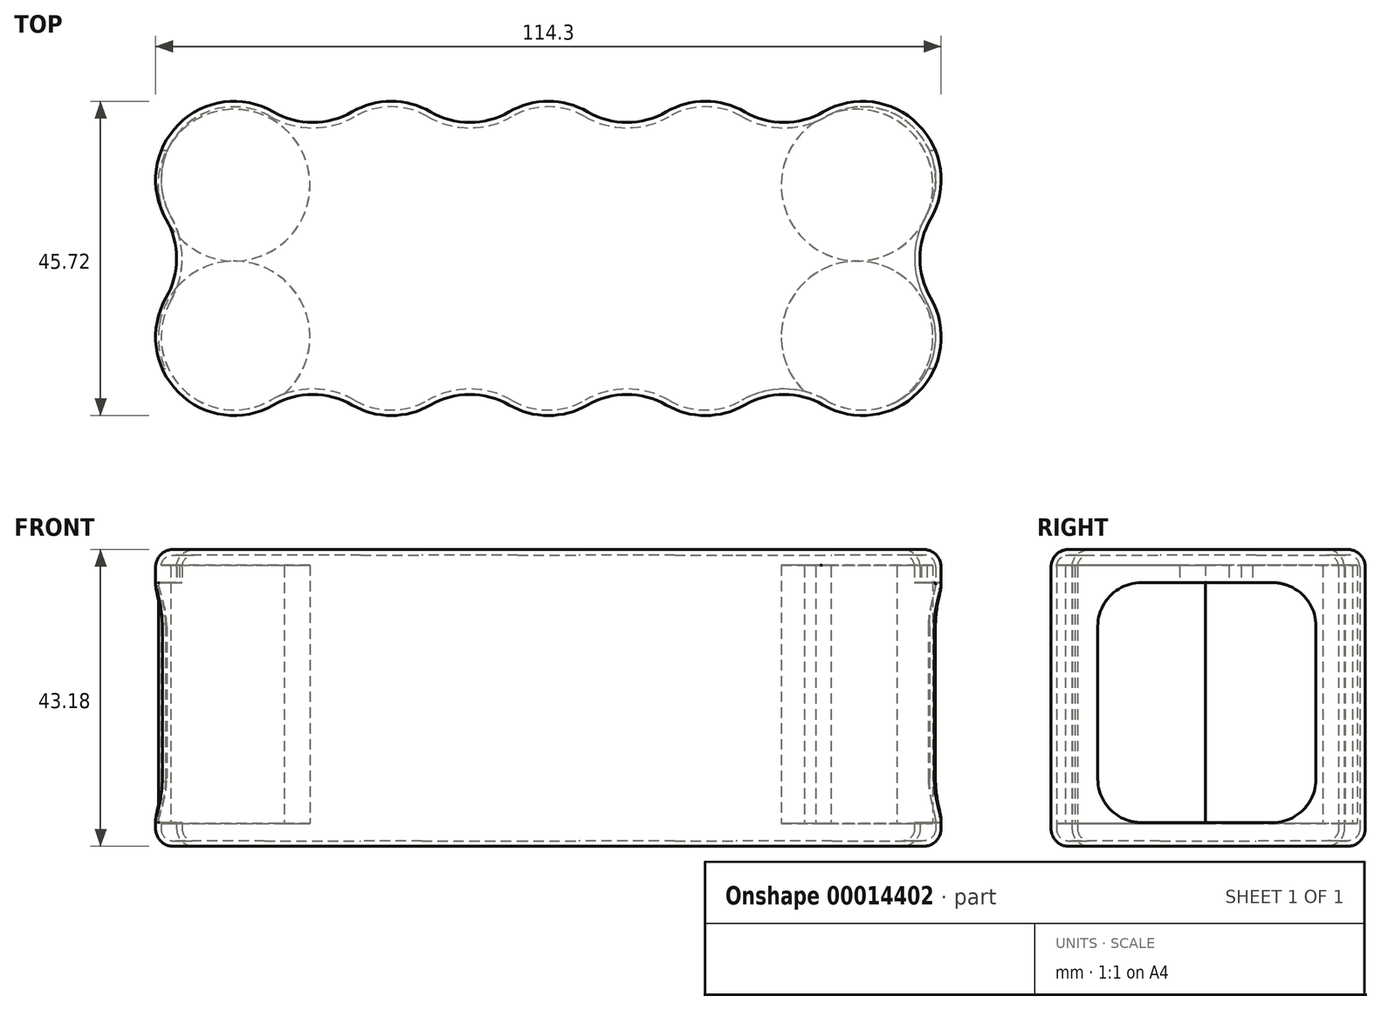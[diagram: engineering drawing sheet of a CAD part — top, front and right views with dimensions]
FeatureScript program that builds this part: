
annotation { "Feature Type Name" : "Feature", "Feature Type Description" : "" }
export const myFeature = defineFeature(function(context is Context, id is Id, definition is map)
    precondition{}
    {
        {
            var Q0;
            Q0=qCreatedBy(makeId("Top.planeOp"),FACE);
            var sketch = newSketch(context, id + "F0", { "sketchPlane" : qUnion([Q0])});
            skArc(sketch, "E0", {"start": v(-9.9, 5.71) * mm, "mid": v(-8.08, -8.08) * mm, "end": v(5.71, -9.9) * mm});
            skArc(sketch, "E1.1.0.0", {"start": v(17.14, -9.9) * mm, "mid": v(22.86, -11.43) * mm, "end": v(28.57, -9.9) * mm});
            skArc(sketch, "E1.2.0.0", {"start": v(40, -9.9) * mm, "mid": v(45.72, -11.43) * mm, "end": v(51.43, -9.9) * mm});
            skArc(sketch, "E1.3.0.0", {"start": v(62.86, -9.9) * mm, "mid": v(68.58, -11.43) * mm, "end": v(74.3, -9.9) * mm});
            skArc(sketch, "E1.4.0.0", {"start": v(85.72, -9.9) * mm, "mid": v(99.52, -8.08) * mm, "end": v(101.34, 5.71) * mm});
            skLineSegment(sketch, "E1.direction1", {"start": v(0, 0) * mm, "end": v(22.86, 0) * mm, "construction": true});
            skArc(sketch, "E2", {"start": v(17.14, -9.9) * mm, "mid": v(11.43, -8.37) * mm, "end": v(5.71, -9.9) * mm});
            skPoint(sketch, "E3.orphan", {"position": v(11.43, 0) * mm});
            skArc(sketch, "E4.1.0.0", {"start": v(40, -9.9) * mm, "mid": v(34.29, -8.37) * mm, "end": v(28.57, -9.9) * mm});
            skArc(sketch, "E4.2.0.0", {"start": v(62.86, -9.9) * mm, "mid": v(57.15, -8.37) * mm, "end": v(51.43, -9.9) * mm});
            skArc(sketch, "E4.3.0.0", {"start": v(85.72, -9.9) * mm, "mid": v(80, -8.37) * mm, "end": v(74.3, -9.9) * mm});
            skLineSegment(sketch, "E5", {"start": v(0, 11.43) * mm, "end": v(91.44, 11.43) * mm, "construction": true});
            skArc(sketch, "E6.0.MirrorCS", {"start": v(17.14, 32.76) * mm, "mid": v(22.86, 34.3) * mm, "end": v(28.57, 32.76) * mm});
            skArc(sketch, "E6.1.MirrorCS", {"start": v(85.72, 32.76) * mm, "mid": v(99.52, 30.94) * mm, "end": v(101.34, 17.15) * mm});
            skPoint(sketch, "E6.2.MirrorP", {"position": v(11.43, 22.86) * mm});
            skArc(sketch, "E6.3.MirrorCS", {"start": v(17.14, 32.76) * mm, "mid": v(11.43, 31.23) * mm, "end": v(5.72, 32.76) * mm});
            skArc(sketch, "E6.4.MirrorCS", {"start": v(62.86, 32.76) * mm, "mid": v(57.15, 31.23) * mm, "end": v(51.43, 32.76) * mm});
            skArc(sketch, "E6.5.MirrorCS", {"start": v(40, 32.76) * mm, "mid": v(45.72, 34.3) * mm, "end": v(51.43, 32.76) * mm});
            skArc(sketch, "E6.6.MirrorCS", {"start": v(62.86, 32.76) * mm, "mid": v(68.58, 34.3) * mm, "end": v(74.3, 32.76) * mm});
            skArc(sketch, "E6.7.MirrorCS", {"start": v(85.72, 32.76) * mm, "mid": v(80, 31.23) * mm, "end": v(74.3, 32.76) * mm});
            skArc(sketch, "E6.8.MirrorCS", {"start": v(40, 32.76) * mm, "mid": v(34.29, 31.23) * mm, "end": v(28.57, 32.76) * mm});
            skArc(sketch, "E6.9.MirrorCS", {"start": v(-9.9, 17.14) * mm, "mid": v(-8.08, 30.94) * mm, "end": v(5.71, 32.76) * mm});
            skArc(sketch, "E7", {"start": v(-9.9, 5.71) * mm, "mid": v(-8.37, 11.43) * mm, "end": v(-9.9, 17.14) * mm});
            skLineSegment(sketch, "E8", {"start": v(45.72, 22.86) * mm, "end": v(45.72, 0) * mm, "construction": true});
            skArc(sketch, "E9.0.MirrorCS", {"start": v(101.34, 5.71) * mm, "mid": v(99.8, 11.43) * mm, "end": v(101.34, 17.15) * mm});
            skSolve(sketch);
        }
        {
            var Q0;
            Q0=qSketchRegion(id+"F0",true);
            extrude(context, id + "F1", {"entities" : qUnion([Q0]), "depth" : 43.18 * mm});
        }
        {
            var Q0;
            Q0=makeQuery(id+"F1.opExtrude","CAP_EDGE",EDGE,{"disambiguationData":[OSD([sQuery(id+"F0.wireOp",EDGE,"E6.6.MirrorCS")])],"isStart":false});
            var Q1;
            Q1=makeQuery(id+"F1.opExtrude","SWEPT_EDGE",EDGE,{"disambiguationData":[OSD([sQuery(id+"F0.wireOp",EDGE,"E6.4.MirrorCS"),sQuery(id+"F0.wireOp",EDGE,"E6.6.MirrorCS")])]});
            var Q2;
            Q2=makeQuery(id+"F1.opExtrude","SWEPT_FACE",FACE,{"disambiguationData":[OSD([sQuery(id+"F0.wireOp",EDGE,"E6.4.MirrorCS")])]});
            var Q3;
            Q3=makeQuery(id+"F1.opExtrude","SWEPT_EDGE",EDGE,{"disambiguationData":[OSD([sQuery(id+"F0.wireOp",EDGE,"E6.5.MirrorCS"),sQuery(id+"F0.wireOp",EDGE,"E6.8.MirrorCS")])]});
            var Q4;
            Q4=makeQuery(id+"F1.opExtrude","SWEPT_FACE",FACE,{"disambiguationData":[OSD([sQuery(id+"F0.wireOp",EDGE,"E9.0.MirrorCS")])]});
            var Q5;
            Q5=makeQuery(id+"F1.opExtrude","CAP_EDGE",EDGE,{"disambiguationData":[OSD([sQuery(id+"F0.wireOp",EDGE,"E6.1.MirrorCS")])],"isStart":true});
            var Q6;
            Q6=makeQuery(id+"F1.opExtrude","CAP_EDGE",EDGE,{"disambiguationData":[OSD([sQuery(id+"F0.wireOp",EDGE,"E1.2.0.0")])],"isStart":true});
            var Q7;
            Q7=makeQuery(id+"F1.opExtrude","SWEPT_FACE",FACE,{"disambiguationData":[OSD([sQuery(id+"F0.wireOp",EDGE,"E0")])]});
            var Q8;
            Q8=makeQuery(id+"F1.opExtrude","SWEPT_FACE",FACE,{"disambiguationData":[OSD([sQuery(id+"F0.wireOp",EDGE,"E6.3.MirrorCS")])]});
            var Q9;
            Q9=makeQuery(id+"F1.opExtrude","SWEPT_EDGE",EDGE,{"disambiguationData":[OSD([sQuery(id+"F0.wireOp",EDGE,"E6.3.MirrorCS"),sQuery(id+"F0.wireOp",EDGE,"E6.9.MirrorCS")])]});
            var Q10;
            Q10=makeQuery(id+"F1.opExtrude","SWEPT_FACE",FACE,{"disambiguationData":[OSD([sQuery(id+"F0.wireOp",EDGE,"E6.5.MirrorCS")])]});
            var Q11;
            Q11=makeQuery(id+"F1.opExtrude","CAP_EDGE",EDGE,{"disambiguationData":[OSD([sQuery(id+"F0.wireOp",EDGE,"E6.7.MirrorCS")])],"isStart":false});
            var Q12;
            Q12=makeQuery(id+"F1.opExtrude","SWEPT_FACE",FACE,{"disambiguationData":[OSD([sQuery(id+"F0.wireOp",EDGE,"E6.7.MirrorCS")])]});
            var Q13;
            Q13=makeQuery(id+"F1.opExtrude","CAP_EDGE",EDGE,{"disambiguationData":[OSD([sQuery(id+"F0.wireOp",EDGE,"E6.3.MirrorCS")])],"isStart":false});
            var Q14;
            Q14=makeQuery(id+"F1.opExtrude","CAP_EDGE",EDGE,{"disambiguationData":[OSD([sQuery(id+"F0.wireOp",EDGE,"E6.5.MirrorCS")])],"isStart":true});
            var Q15;
            Q15=makeQuery(id+"F1.opExtrude","SWEPT_FACE",FACE,{"disambiguationData":[OSD([sQuery(id+"F0.wireOp",EDGE,"E6.9.MirrorCS")])]});
            var Q16;
            Q16=makeQuery(id+"F1.opExtrude","CAP_EDGE",EDGE,{"disambiguationData":[OSD([sQuery(id+"F0.wireOp",EDGE,"E0")])],"isStart":true});
            var Q17;
            Q17=makeQuery(id+"F1.opExtrude","CAP_EDGE",EDGE,{"disambiguationData":[OSD([sQuery(id+"F0.wireOp",EDGE,"E6.8.MirrorCS")])],"isStart":true});
            var Q18;
            Q18=makeQuery(id+"F1.opExtrude","SWEPT_FACE",FACE,{"disambiguationData":[OSD([sQuery(id+"F0.wireOp",EDGE,"E6.1.MirrorCS")])]});
            var Q19;
            Q19=makeQuery(id+"F1.opExtrude","SWEPT_FACE",FACE,{"disambiguationData":[OSD([sQuery(id+"F0.wireOp",EDGE,"E6.0.MirrorCS")])]});
            var Q20;
            Q20=makeQuery(id+"F1.opExtrude","CAP_EDGE",EDGE,{"disambiguationData":[OSD([sQuery(id+"F0.wireOp",EDGE,"E6.1.MirrorCS")])],"isStart":false});
            var Q21;
            Q21=makeQuery(id+"F1.opExtrude","SWEPT_FACE",FACE,{"disambiguationData":[OSD([sQuery(id+"F0.wireOp",EDGE,"E4.3.0.0")])]});
            var Q22;
            Q22=makeQuery(id+"F1.opExtrude","SWEPT_EDGE",EDGE,{"disambiguationData":[OSD([sQuery(id+"F0.wireOp",EDGE,"E6.0.MirrorCS"),sQuery(id+"F0.wireOp",EDGE,"E6.3.MirrorCS")])]});
            var Q23;
            Q23=makeQuery(id+"F1.opExtrude","SWEPT_FACE",FACE,{"disambiguationData":[OSD([sQuery(id+"F0.wireOp",EDGE,"E4.2.0.0")])]});
            var Q24;
            Q24=makeQuery(id+"F1.opExtrude","CAP_EDGE",EDGE,{"disambiguationData":[OSD([sQuery(id+"F0.wireOp",EDGE,"E6.9.MirrorCS")])],"isStart":false});
            var Q25;
            Q25=makeQuery(id+"F1.opExtrude","SWEPT_FACE",FACE,{"disambiguationData":[OSD([sQuery(id+"F0.wireOp",EDGE,"E4.1.0.0")])]});
            var Q26;
            Q26=makeQuery(id+"F1.opExtrude","CAP_EDGE",EDGE,{"disambiguationData":[OSD([sQuery(id+"F0.wireOp",EDGE,"E6.9.MirrorCS")])],"isStart":true});
            var Q27;
            Q27=makeQuery(id+"F1.opExtrude","CAP_EDGE",EDGE,{"disambiguationData":[OSD([sQuery(id+"F0.wireOp",EDGE,"E6.0.MirrorCS")])],"isStart":true});
            var Q28;
            Q28=makeQuery(id+"F1.opExtrude","SWEPT_FACE",FACE,{"disambiguationData":[OSD([sQuery(id+"F0.wireOp",EDGE,"E2")])]});
            var Q29;
            Q29=makeQuery(id+"F1.opExtrude","SWEPT_FACE",FACE,{"disambiguationData":[OSD([sQuery(id+"F0.wireOp",EDGE,"E1.4.0.0")])]});
            var Q30;
            Q30=makeQuery(id+"F1.opExtrude","SWEPT_FACE",FACE,{"disambiguationData":[OSD([sQuery(id+"F0.wireOp",EDGE,"E7")])]});
            var Q31;
            Q31=makeQuery(id+"F1.opExtrude","CAP_FACE",FACE,{"disambiguationData":[OSD([sQuery(id+"F0.wireOp",EDGE,"E0"),sQuery(id+"F0.wireOp",EDGE,"E1.1.0.0"),sQuery(id+"F0.wireOp",EDGE,"E1.2.0.0"),sQuery(id+"F0.wireOp",EDGE,"E1.3.0.0"),sQuery(id+"F0.wireOp",EDGE,"E1.4.0.0"),sQuery(id+"F0.wireOp",EDGE,"E2"),sQuery(id+"F0.wireOp",EDGE,"E4.1.0.0"),sQuery(id+"F0.wireOp",EDGE,"E4.2.0.0"),sQuery(id+"F0.wireOp",EDGE,"E4.3.0.0"),sQuery(id+"F0.wireOp",EDGE,"E6.0.MirrorCS"),sQuery(id+"F0.wireOp",EDGE,"E6.1.MirrorCS"),sQuery(id+"F0.wireOp",EDGE,"E6.3.MirrorCS"),sQuery(id+"F0.wireOp",EDGE,"E6.4.MirrorCS"),sQuery(id+"F0.wireOp",EDGE,"E6.5.MirrorCS"),sQuery(id+"F0.wireOp",EDGE,"E6.6.MirrorCS"),sQuery(id+"F0.wireOp",EDGE,"E6.7.MirrorCS"),sQuery(id+"F0.wireOp",EDGE,"E6.8.MirrorCS"),sQuery(id+"F0.wireOp",EDGE,"E6.9.MirrorCS"),sQuery(id+"F0.wireOp",EDGE,"E7"),sQuery(id+"F0.wireOp",EDGE,"E9.0.MirrorCS")])],"isStart":false});
            var Q32;
            Q32=makeQuery(id+"F1.opExtrude","CAP_FACE",FACE,{"disambiguationData":[OSD([sQuery(id+"F0.wireOp",EDGE,"E0"),sQuery(id+"F0.wireOp",EDGE,"E1.1.0.0"),sQuery(id+"F0.wireOp",EDGE,"E1.2.0.0"),sQuery(id+"F0.wireOp",EDGE,"E1.3.0.0"),sQuery(id+"F0.wireOp",EDGE,"E1.4.0.0"),sQuery(id+"F0.wireOp",EDGE,"E2"),sQuery(id+"F0.wireOp",EDGE,"E4.1.0.0"),sQuery(id+"F0.wireOp",EDGE,"E4.2.0.0"),sQuery(id+"F0.wireOp",EDGE,"E4.3.0.0"),sQuery(id+"F0.wireOp",EDGE,"E6.0.MirrorCS"),sQuery(id+"F0.wireOp",EDGE,"E6.1.MirrorCS"),sQuery(id+"F0.wireOp",EDGE,"E6.3.MirrorCS"),sQuery(id+"F0.wireOp",EDGE,"E6.4.MirrorCS"),sQuery(id+"F0.wireOp",EDGE,"E6.5.MirrorCS"),sQuery(id+"F0.wireOp",EDGE,"E6.6.MirrorCS"),sQuery(id+"F0.wireOp",EDGE,"E6.7.MirrorCS"),sQuery(id+"F0.wireOp",EDGE,"E6.8.MirrorCS"),sQuery(id+"F0.wireOp",EDGE,"E6.9.MirrorCS"),sQuery(id+"F0.wireOp",EDGE,"E7"),sQuery(id+"F0.wireOp",EDGE,"E9.0.MirrorCS")])],"isStart":true});
            var Q33;
            Q33=makeQuery(id+"F1.opExtrude","CAP_EDGE",EDGE,{"disambiguationData":[OSD([sQuery(id+"F0.wireOp",EDGE,"E6.8.MirrorCS")])],"isStart":false});
            var Q34;
            Q34=makeQuery(id+"F1.opExtrude","CAP_EDGE",EDGE,{"disambiguationData":[OSD([sQuery(id+"F0.wireOp",EDGE,"E6.3.MirrorCS")])],"isStart":true});
            var Q35;
            Q35=makeQuery(id+"F1.opExtrude","CAP_EDGE",EDGE,{"disambiguationData":[OSD([sQuery(id+"F0.wireOp",EDGE,"E6.4.MirrorCS")])],"isStart":false});
            var Q36;
            Q36=makeQuery(id+"F1.opExtrude","SWEPT_FACE",FACE,{"disambiguationData":[OSD([sQuery(id+"F0.wireOp",EDGE,"E6.8.MirrorCS")])]});
            var Q37;
            Q37=makeQuery(id+"F1.opExtrude","SWEPT_FACE",FACE,{"disambiguationData":[OSD([sQuery(id+"F0.wireOp",EDGE,"E6.6.MirrorCS")])]});
            var Q38;
            Q38=makeQuery(id+"F1.opExtrude","CAP_EDGE",EDGE,{"disambiguationData":[OSD([sQuery(id+"F0.wireOp",EDGE,"E1.4.0.0")])],"isStart":true});
            var Q39;
            Q39=makeQuery(id+"F1.opExtrude","CAP_EDGE",EDGE,{"disambiguationData":[OSD([sQuery(id+"F0.wireOp",EDGE,"E6.4.MirrorCS")])],"isStart":true});
            var Q40;
            Q40=makeQuery(id+"F1.opExtrude","CAP_EDGE",EDGE,{"disambiguationData":[OSD([sQuery(id+"F0.wireOp",EDGE,"E6.5.MirrorCS")])],"isStart":false});
            var Q41;
            Q41=makeQuery(id+"F1.opExtrude","SWEPT_EDGE",EDGE,{"disambiguationData":[OSD([sQuery(id+"F0.wireOp",EDGE,"E6.6.MirrorCS"),sQuery(id+"F0.wireOp",EDGE,"E6.7.MirrorCS")])]});
            var Q42;
            Q42=makeQuery(id+"F1.opExtrude","CAP_EDGE",EDGE,{"disambiguationData":[OSD([sQuery(id+"F0.wireOp",EDGE,"E6.7.MirrorCS")])],"isStart":true});
            var Q43;
            Q43=makeQuery(id+"F1.opExtrude","CAP_EDGE",EDGE,{"disambiguationData":[OSD([sQuery(id+"F0.wireOp",EDGE,"E6.6.MirrorCS")])],"isStart":true});
            var Q44;
            Q44=makeQuery(id+"F1.opExtrude","SWEPT_EDGE",EDGE,{"disambiguationData":[OSD([sQuery(id+"F0.wireOp",EDGE,"E6.1.MirrorCS"),sQuery(id+"F0.wireOp",EDGE,"E9.0.MirrorCS")])]});
            var Q45;
            Q45=makeQuery(id+"F1.opExtrude","CAP_EDGE",EDGE,{"disambiguationData":[OSD([sQuery(id+"F0.wireOp",EDGE,"E4.1.0.0")])],"isStart":false});
            var Q46;
            Q46=makeQuery(id+"F1.opExtrude","CAP_EDGE",EDGE,{"disambiguationData":[OSD([sQuery(id+"F0.wireOp",EDGE,"E1.3.0.0")])],"isStart":true});
            var Q47;
            Q47=makeQuery(id+"F1.opExtrude","CAP_EDGE",EDGE,{"disambiguationData":[OSD([sQuery(id+"F0.wireOp",EDGE,"E7")])],"isStart":true});
            var Q48;
            Q48=makeQuery(id+"F1.opExtrude","SWEPT_EDGE",EDGE,{"disambiguationData":[OSD([sQuery(id+"F0.wireOp",EDGE,"E0"),sQuery(id+"F0.wireOp",EDGE,"E7")])]});
            var Q49;
            Q49=makeQuery(id+"F1.opExtrude","CAP_EDGE",EDGE,{"disambiguationData":[OSD([sQuery(id+"F0.wireOp",EDGE,"E4.2.0.0")])],"isStart":false});
            var Q50;
            Q50=makeQuery(id+"F1.opExtrude","SWEPT_EDGE",EDGE,{"disambiguationData":[OSD([sQuery(id+"F0.wireOp",EDGE,"E6.9.MirrorCS"),sQuery(id+"F0.wireOp",EDGE,"E7")])]});
            var Q51;
            Q51=makeQuery(id+"F1.opExtrude","CAP_EDGE",EDGE,{"disambiguationData":[OSD([sQuery(id+"F0.wireOp",EDGE,"E9.0.MirrorCS")])],"isStart":false});
            var Q52;
            Q52=makeQuery(id+"F1.opExtrude","CAP_EDGE",EDGE,{"disambiguationData":[OSD([sQuery(id+"F0.wireOp",EDGE,"E1.3.0.0")])],"isStart":false});
            var Q53;
            Q53=makeQuery(id+"F1.opExtrude","CAP_EDGE",EDGE,{"disambiguationData":[OSD([sQuery(id+"F0.wireOp",EDGE,"E2")])],"isStart":true});
            var Q54;
            Q54=makeQuery(id+"F1.opExtrude","CAP_EDGE",EDGE,{"disambiguationData":[OSD([sQuery(id+"F0.wireOp",EDGE,"E4.3.0.0")])],"isStart":true});
            var Q55;
            Q55=makeQuery(id+"F1.opExtrude","SWEPT_EDGE",EDGE,{"disambiguationData":[OSD([sQuery(id+"F0.wireOp",EDGE,"E6.1.MirrorCS"),sQuery(id+"F0.wireOp",EDGE,"E6.7.MirrorCS")])]});
            var Q56;
            Q56=makeQuery(id+"F1.opExtrude","SWEPT_EDGE",EDGE,{"disambiguationData":[OSD([sQuery(id+"F0.wireOp",EDGE,"E6.0.MirrorCS"),sQuery(id+"F0.wireOp",EDGE,"E6.8.MirrorCS")])]});
            var Q57;
            Q57=makeQuery(id+"F1.opExtrude","CAP_EDGE",EDGE,{"disambiguationData":[OSD([sQuery(id+"F0.wireOp",EDGE,"E1.2.0.0")])],"isStart":false});
            var Q58;
            Q58=makeQuery(id+"F1.opExtrude","CAP_EDGE",EDGE,{"disambiguationData":[OSD([sQuery(id+"F0.wireOp",EDGE,"E7")])],"isStart":false});
            var Q59;
            Q59=makeQuery(id+"F1.opExtrude","CAP_EDGE",EDGE,{"disambiguationData":[OSD([sQuery(id+"F0.wireOp",EDGE,"E1.1.0.0")])],"isStart":false});
            var Q60;
            Q60=makeQuery(id+"F1.opExtrude","SWEPT_EDGE",EDGE,{"disambiguationData":[OSD([sQuery(id+"F0.wireOp",EDGE,"E1.4.0.0"),sQuery(id+"F0.wireOp",EDGE,"E9.0.MirrorCS")])]});
            var Q61;
            Q61=makeQuery(id+"F1.opExtrude","SWEPT_EDGE",EDGE,{"disambiguationData":[OSD([sQuery(id+"F0.wireOp",EDGE,"E1.4.0.0"),sQuery(id+"F0.wireOp",EDGE,"E4.3.0.0")])]});
            var Q62;
            Q62=makeQuery(id+"F1.opExtrude","CAP_EDGE",EDGE,{"disambiguationData":[OSD([sQuery(id+"F0.wireOp",EDGE,"E6.0.MirrorCS")])],"isStart":false});
            var Q63;
            Q63=makeQuery(id+"F1.opExtrude","SWEPT_EDGE",EDGE,{"disambiguationData":[OSD([sQuery(id+"F0.wireOp",EDGE,"E1.3.0.0"),sQuery(id+"F0.wireOp",EDGE,"E4.3.0.0")])]});
            var Q64;
            Q64=makeQuery(id+"F1.opExtrude","CAP_EDGE",EDGE,{"disambiguationData":[OSD([sQuery(id+"F0.wireOp",EDGE,"E1.1.0.0")])],"isStart":true});
            var Q65;
            Q65=makeQuery(id+"F1.opExtrude","SWEPT_EDGE",EDGE,{"disambiguationData":[OSD([sQuery(id+"F0.wireOp",EDGE,"E1.3.0.0"),sQuery(id+"F0.wireOp",EDGE,"E4.2.0.0")])]});
            var Q66;
            Q66=makeQuery(id+"F1.opExtrude","SWEPT_FACE",FACE,{"disambiguationData":[OSD([sQuery(id+"F0.wireOp",EDGE,"E1.3.0.0")])]});
            var Q67;
            Q67=makeQuery(id+"F1.opExtrude","SWEPT_FACE",FACE,{"disambiguationData":[OSD([sQuery(id+"F0.wireOp",EDGE,"E1.2.0.0")])]});
            var Q68;
            Q68=makeQuery(id+"F1.opExtrude","SWEPT_EDGE",EDGE,{"disambiguationData":[OSD([sQuery(id+"F0.wireOp",EDGE,"E1.2.0.0"),sQuery(id+"F0.wireOp",EDGE,"E4.1.0.0")])]});
            var Q69;
            Q69=makeQuery(id+"F1.opExtrude","SWEPT_FACE",FACE,{"disambiguationData":[OSD([sQuery(id+"F0.wireOp",EDGE,"E1.1.0.0")])]});
            var Q70;
            Q70=makeQuery(id+"F1.opExtrude","SWEPT_EDGE",EDGE,{"disambiguationData":[OSD([sQuery(id+"F0.wireOp",EDGE,"E1.1.0.0"),sQuery(id+"F0.wireOp",EDGE,"E4.1.0.0")])]});
            var Q71;
            Q71=makeQuery(id+"F1.opExtrude","SWEPT_EDGE",EDGE,{"disambiguationData":[OSD([sQuery(id+"F0.wireOp",EDGE,"E1.1.0.0"),sQuery(id+"F0.wireOp",EDGE,"E2")])]});
            var Q72;
            Q72=makeQuery(id+"F1.opExtrude","SWEPT_EDGE",EDGE,{"disambiguationData":[OSD([sQuery(id+"F0.wireOp",EDGE,"E0"),sQuery(id+"F0.wireOp",EDGE,"E2")])]});
            var Q73;
            Q73=makeQuery(id+"F1.opExtrude","CAP_EDGE",EDGE,{"disambiguationData":[OSD([sQuery(id+"F0.wireOp",EDGE,"E4.3.0.0")])],"isStart":false});
            var Q74;
            Q74=makeQuery(id+"F1.opExtrude","CAP_EDGE",EDGE,{"disambiguationData":[OSD([sQuery(id+"F0.wireOp",EDGE,"E0")])],"isStart":false});
            var Q75;
            Q75=makeQuery(id+"F1.opExtrude","CAP_EDGE",EDGE,{"disambiguationData":[OSD([sQuery(id+"F0.wireOp",EDGE,"E9.0.MirrorCS")])],"isStart":true});
            var Q76;
            Q76=makeQuery(id+"F1.opExtrude","CAP_EDGE",EDGE,{"disambiguationData":[OSD([sQuery(id+"F0.wireOp",EDGE,"E1.4.0.0")])],"isStart":false});
            var Q77;
            Q77=makeQuery(id+"F1.opExtrude","CAP_EDGE",EDGE,{"disambiguationData":[OSD([sQuery(id+"F0.wireOp",EDGE,"E2")])],"isStart":false});
            var Q78;
            Q78=makeQuery(id+"F1.opExtrude","CAP_EDGE",EDGE,{"disambiguationData":[OSD([sQuery(id+"F0.wireOp",EDGE,"E4.2.0.0")])],"isStart":true});
            var Q79;
            Q79=makeQuery(id+"F1.opExtrude","CAP_EDGE",EDGE,{"disambiguationData":[OSD([sQuery(id+"F0.wireOp",EDGE,"E4.1.0.0")])],"isStart":true});
            var Q80;
            Q80=makeQuery(id+"F1.opExtrude","SWEPT_EDGE",EDGE,{"disambiguationData":[OSD([sQuery(id+"F0.wireOp",EDGE,"E6.4.MirrorCS"),sQuery(id+"F0.wireOp",EDGE,"E6.5.MirrorCS")])]});
            var Q81;
            Q81=makeQuery(id+"F1.opExtrude","SWEPT_EDGE",EDGE,{"disambiguationData":[OSD([sQuery(id+"F0.wireOp",EDGE,"E1.2.0.0"),sQuery(id+"F0.wireOp",EDGE,"E4.2.0.0")])]});
            fillet(context, id + "F2", {"entities" : qUnion([Q0, Q1, Q2, Q3, Q4, Q5, Q6, Q7, Q8, Q9, Q10, Q11, Q12, Q13, Q14, Q15, Q16, Q17, Q18, Q19, Q20, Q21, Q22, Q23, Q24, Q25, Q26, Q27, Q28, Q29, Q30, Q31, Q32, Q33, Q34, Q35, Q36, Q37, Q38, Q39, Q40, Q41, Q42, Q43, Q44, Q45, Q46, Q47, Q48, Q49, Q50, Q51, Q52, Q53, Q54, Q55, Q56, Q57, Q58, Q59, Q60, Q61, Q62, Q63, Q64, Q65, Q66, Q67, Q68, Q69, Q70, Q71, Q72, Q73, Q74, Q75, Q76, Q77, Q78, Q79, Q80, Q81]), "radius" : 2.54 * mm, "tangentPropagation" : true, "allowEdgeOverflow" : false});
        }
        {
            var Q0;
            Q0=qCreatedBy(makeId("Right.planeOp"),FACE);
            var sketch = newSketch(context, id + "F3", { "sketchPlane" : qUnion([Q0])});
            skLineSegment(sketch, "E10.bottom", {"start": v(1.73, 3.44) * mm, "end": v(20.78, 3.44) * mm});
            skLineSegment(sketch, "E10.top", {"start": v(1.73, 38.37) * mm, "end": v(20.78, 38.37) * mm});
            skLineSegment(sketch, "E10.left", {"start": v(-4.62, 9.8) * mm, "end": v(-4.62, 32.02) * mm});
            skLineSegment(sketch, "E10.right", {"start": v(27.13, 9.8) * mm, "end": v(27.13, 32.02) * mm});
            skPoint(sketch, "E11.visualSharp", {"position": v(-4.62, 3.44) * mm});
            skArc(sketch, "E11.filletArc", {"start": v(-4.62, 9.8) * mm, "mid": v(-2.76, 5.3) * mm, "end": v(1.73, 3.44) * mm});
            skPoint(sketch, "E12.visualSharp", {"position": v(27.13, 3.44) * mm});
            skArc(sketch, "E12.filletArc", {"start": v(20.78, 3.44) * mm, "mid": v(25.27, 5.3) * mm, "end": v(27.13, 9.8) * mm});
            skPoint(sketch, "E13.visualSharp", {"position": v(27.13, 38.37) * mm});
            skArc(sketch, "E13.filletArc", {"start": v(27.13, 32.02) * mm, "mid": v(25.27, 36.5) * mm, "end": v(20.78, 38.37) * mm});
            skPoint(sketch, "E14.visualSharp", {"position": v(-4.62, 38.37) * mm});
            skArc(sketch, "E14.filletArc", {"start": v(1.73, 38.37) * mm, "mid": v(-2.76, 36.5) * mm, "end": v(-4.62, 32.02) * mm});
            skSolve(sketch);
        }
        {
            var Q0;
            {var subQ0=sQuery(id+"F0.wireOp",EDGE,"E7");Q0=makeQuery(id+"F2.opFillet","BLEND_FACE",FACE,{"disambiguationData":[OSD([subQ0]),TDD([makeQuery(id+"F1.opExtrude","CAP_EDGE",EDGE,{"disambiguationData":[OSD([subQ0])],"isStart":true})])]});}
            var Q1;
            {var subQ0=sQuery(id+"F0.wireOp",EDGE,"E7");Q1=makeQuery(id+"F2.opFillet","BLEND_FACE",FACE,{"disambiguationData":[OSD([subQ0]),TDD([makeQuery(id+"F1.opExtrude","CAP_EDGE",EDGE,{"disambiguationData":[OSD([subQ0])],"isStart":false})])]});}
            var Q2;
            Q2=makeQuery(id+"F1.opExtrude","CAP_FACE",FACE,{"disambiguationData":[OSD([sQuery(id+"F0.wireOp",EDGE,"E0"),sQuery(id+"F0.wireOp",EDGE,"E1.1.0.0"),sQuery(id+"F0.wireOp",EDGE,"E1.2.0.0"),sQuery(id+"F0.wireOp",EDGE,"E1.3.0.0"),sQuery(id+"F0.wireOp",EDGE,"E1.4.0.0"),sQuery(id+"F0.wireOp",EDGE,"E2"),sQuery(id+"F0.wireOp",EDGE,"E4.1.0.0"),sQuery(id+"F0.wireOp",EDGE,"E4.2.0.0"),sQuery(id+"F0.wireOp",EDGE,"E4.3.0.0"),sQuery(id+"F0.wireOp",EDGE,"E6.0.MirrorCS"),sQuery(id+"F0.wireOp",EDGE,"E6.1.MirrorCS"),sQuery(id+"F0.wireOp",EDGE,"E6.3.MirrorCS"),sQuery(id+"F0.wireOp",EDGE,"E6.4.MirrorCS"),sQuery(id+"F0.wireOp",EDGE,"E6.5.MirrorCS"),sQuery(id+"F0.wireOp",EDGE,"E6.6.MirrorCS"),sQuery(id+"F0.wireOp",EDGE,"E6.7.MirrorCS"),sQuery(id+"F0.wireOp",EDGE,"E6.8.MirrorCS"),sQuery(id+"F0.wireOp",EDGE,"E6.9.MirrorCS"),sQuery(id+"F0.wireOp",EDGE,"E7"),sQuery(id+"F0.wireOp",EDGE,"E9.0.MirrorCS")])],"isStart":true});
            var Q3;
            {var subQ0=sQuery(id+"F0.wireOp",EDGE,"E6.9.MirrorCS");Q3=makeQuery(id+"F2.opFillet","BLEND_FACE",FACE,{"disambiguationData":[OSD([subQ0]),TDD([makeQuery(id+"F1.opExtrude","CAP_EDGE",EDGE,{"disambiguationData":[OSD([subQ0])],"isStart":true})])]});}
            var Q4;
            {var subQ0=sQuery(id+"F0.wireOp",EDGE,"E6.9.MirrorCS");Q4=makeQuery(id+"F2.opFillet","BLEND_FACE",FACE,{"disambiguationData":[OSD([subQ0]),TDD([makeQuery(id+"F1.opExtrude","CAP_EDGE",EDGE,{"disambiguationData":[OSD([subQ0])],"isStart":false})])]});}
            var Q5;
            {var subQ0=sQuery(id+"F0.wireOp",EDGE,"E0");Q5=makeQuery(id+"F2.opFillet","BLEND_FACE",FACE,{"disambiguationData":[OSD([subQ0]),TDD([makeQuery(id+"F1.opExtrude","CAP_EDGE",EDGE,{"disambiguationData":[OSD([subQ0])],"isStart":false})])]});}
            var Q6;
            Q6=makeQuery(id+"F1.opExtrude","SWEPT_FACE",FACE,{"disambiguationData":[OSD([sQuery(id+"F0.wireOp",EDGE,"E7")])]});
            var Q7;
            Q7=makeQuery(id+"F1.opExtrude","SWEPT_FACE",FACE,{"disambiguationData":[OSD([sQuery(id+"F0.wireOp",EDGE,"E0")])]});
            var Q8;
            Q8=makeQuery(id+"F1.opExtrude","SWEPT_FACE",FACE,{"disambiguationData":[OSD([sQuery(id+"F0.wireOp",EDGE,"E6.9.MirrorCS")])]});
            var Q9;
            Q9=makeQuery(id+"F1.opExtrude","SWEPT_FACE",FACE,{"disambiguationData":[OSD([sQuery(id+"F0.wireOp",EDGE,"E6.6.MirrorCS")])]});
            var Q10;
            {var subQ0=sQuery(id+"F0.wireOp",EDGE,"E6.8.MirrorCS");Q10=makeQuery(id+"F2.opFillet","BLEND_FACE",FACE,{"disambiguationData":[OSD([subQ0]),TDD([makeQuery(id+"F1.opExtrude","CAP_EDGE",EDGE,{"disambiguationData":[OSD([subQ0])],"isStart":false})])]});}
            var Q11;
            Q11=makeQuery(id+"F1.opExtrude","SWEPT_FACE",FACE,{"disambiguationData":[OSD([sQuery(id+"F0.wireOp",EDGE,"E4.2.0.0")])]});
            var Q12;
            {var subQ0=sQuery(id+"F0.wireOp",EDGE,"E6.7.MirrorCS");Q12=makeQuery(id+"F2.opFillet","BLEND_FACE",FACE,{"disambiguationData":[OSD([subQ0]),TDD([makeQuery(id+"F1.opExtrude","CAP_EDGE",EDGE,{"disambiguationData":[OSD([subQ0])],"isStart":false})])]});}
            var Q13;
            {var subQ0=sQuery(id+"F0.wireOp",EDGE,"E6.1.MirrorCS");Q13=makeQuery(id+"F2.opFillet","BLEND_FACE",FACE,{"disambiguationData":[OSD([subQ0]),TDD([makeQuery(id+"F1.opExtrude","CAP_EDGE",EDGE,{"disambiguationData":[OSD([subQ0])],"isStart":false})])]});}
            var Q14;
            Q14=makeQuery(id+"F1.opExtrude","SWEPT_FACE",FACE,{"disambiguationData":[OSD([sQuery(id+"F0.wireOp",EDGE,"E6.3.MirrorCS")])]});
            var Q15;
            {var subQ0=sQuery(id+"F0.wireOp",EDGE,"E6.6.MirrorCS");Q15=makeQuery(id+"F2.opFillet","BLEND_FACE",FACE,{"disambiguationData":[OSD([subQ0]),TDD([makeQuery(id+"F1.opExtrude","CAP_EDGE",EDGE,{"disambiguationData":[OSD([subQ0])],"isStart":false})])]});}
            var Q16;
            Q16=makeQuery(id+"F1.opExtrude","SWEPT_FACE",FACE,{"disambiguationData":[OSD([sQuery(id+"F0.wireOp",EDGE,"E1.3.0.0")])]});
            var Q17;
            {var subQ0=sQuery(id+"F0.wireOp",EDGE,"E6.7.MirrorCS");Q17=makeQuery(id+"F2.opFillet","BLEND_FACE",FACE,{"disambiguationData":[OSD([subQ0]),TDD([makeQuery(id+"F1.opExtrude","CAP_EDGE",EDGE,{"disambiguationData":[OSD([subQ0])],"isStart":true})])]});}
            var Q18;
            {var subQ0=sQuery(id+"F0.wireOp",EDGE,"E6.6.MirrorCS");Q18=makeQuery(id+"F2.opFillet","BLEND_FACE",FACE,{"disambiguationData":[OSD([subQ0]),TDD([makeQuery(id+"F1.opExtrude","CAP_EDGE",EDGE,{"disambiguationData":[OSD([subQ0])],"isStart":true})])]});}
            var Q19;
            Q19=makeQuery(id+"F1.opExtrude","SWEPT_FACE",FACE,{"disambiguationData":[OSD([sQuery(id+"F0.wireOp",EDGE,"E1.1.0.0")])]});
            var Q20;
            Q20=makeQuery(id+"F1.opExtrude","SWEPT_FACE",FACE,{"disambiguationData":[OSD([sQuery(id+"F0.wireOp",EDGE,"E1.2.0.0")])]});
            var Q21;
            {var subQ0=sQuery(id+"F0.wireOp",EDGE,"E6.4.MirrorCS");Q21=makeQuery(id+"F2.opFillet","BLEND_FACE",FACE,{"disambiguationData":[OSD([subQ0]),TDD([makeQuery(id+"F1.opExtrude","CAP_EDGE",EDGE,{"disambiguationData":[OSD([subQ0])],"isStart":true})])]});}
            var Q22;
            {var subQ0=sQuery(id+"F0.wireOp",EDGE,"E6.1.MirrorCS");Q22=makeQuery(id+"F2.opFillet","BLEND_FACE",FACE,{"disambiguationData":[OSD([subQ0]),TDD([makeQuery(id+"F1.opExtrude","CAP_EDGE",EDGE,{"disambiguationData":[OSD([subQ0])],"isStart":true})])]});}
            var Q23;
            {var subQ0=sQuery(id+"F0.wireOp",EDGE,"E6.3.MirrorCS");Q23=makeQuery(id+"F2.opFillet","BLEND_FACE",FACE,{"disambiguationData":[OSD([subQ0]),TDD([makeQuery(id+"F1.opExtrude","CAP_EDGE",EDGE,{"disambiguationData":[OSD([subQ0])],"isStart":true})])]});}
            var Q24;
            {var subQ0=sQuery(id+"F0.wireOp",EDGE,"E9.0.MirrorCS");Q24=makeQuery(id+"F2.opFillet","BLEND_FACE",FACE,{"disambiguationData":[OSD([subQ0]),TDD([makeQuery(id+"F1.opExtrude","CAP_EDGE",EDGE,{"disambiguationData":[OSD([subQ0])],"isStart":true})])]});}
            var Q25;
            Q25=makeQuery(id+"F1.opExtrude","SWEPT_FACE",FACE,{"disambiguationData":[OSD([sQuery(id+"F0.wireOp",EDGE,"E6.4.MirrorCS")])]});
            var Q26;
            Q26=makeQuery(id+"F1.opExtrude","SWEPT_FACE",FACE,{"disambiguationData":[OSD([sQuery(id+"F0.wireOp",EDGE,"E2")])]});
            var Q27;
            {var subQ0=sQuery(id+"F0.wireOp",EDGE,"E6.5.MirrorCS");Q27=makeQuery(id+"F2.opFillet","BLEND_FACE",FACE,{"disambiguationData":[OSD([subQ0]),TDD([makeQuery(id+"F1.opExtrude","CAP_EDGE",EDGE,{"disambiguationData":[OSD([subQ0])],"isStart":false})])]});}
            var Q28;
            {var subQ0=sQuery(id+"F0.wireOp",EDGE,"E6.8.MirrorCS");Q28=makeQuery(id+"F2.opFillet","BLEND_FACE",FACE,{"disambiguationData":[OSD([subQ0]),TDD([makeQuery(id+"F1.opExtrude","CAP_EDGE",EDGE,{"disambiguationData":[OSD([subQ0])],"isStart":true})])]});}
            var Q29;
            Q29=makeQuery(id+"F1.opExtrude","SWEPT_FACE",FACE,{"disambiguationData":[OSD([sQuery(id+"F0.wireOp",EDGE,"E4.1.0.0")])]});
            var Q30;
            {var subQ0=sQuery(id+"F0.wireOp",EDGE,"E4.3.0.0");Q30=makeQuery(id+"F2.opFillet","BLEND_FACE",FACE,{"disambiguationData":[OSD([subQ0]),TDD([makeQuery(id+"F1.opExtrude","CAP_EDGE",EDGE,{"disambiguationData":[OSD([subQ0])],"isStart":true})])]});}
            var Q31;
            Q31=makeQuery(id+"F1.opExtrude","SWEPT_FACE",FACE,{"disambiguationData":[OSD([sQuery(id+"F0.wireOp",EDGE,"E6.7.MirrorCS")])]});
            var Q32;
            {var subQ0=sQuery(id+"F0.wireOp",EDGE,"E6.4.MirrorCS");Q32=makeQuery(id+"F2.opFillet","BLEND_FACE",FACE,{"disambiguationData":[OSD([subQ0]),TDD([makeQuery(id+"F1.opExtrude","CAP_EDGE",EDGE,{"disambiguationData":[OSD([subQ0])],"isStart":false})])]});}
            var Q33;
            Q33=makeQuery(id+"F1.opExtrude","SWEPT_FACE",FACE,{"disambiguationData":[OSD([sQuery(id+"F0.wireOp",EDGE,"E4.3.0.0")])]});
            var Q34;
            {var subQ0=sQuery(id+"F0.wireOp",EDGE,"E6.0.MirrorCS");Q34=makeQuery(id+"F2.opFillet","BLEND_FACE",FACE,{"disambiguationData":[OSD([subQ0]),TDD([makeQuery(id+"F1.opExtrude","CAP_EDGE",EDGE,{"disambiguationData":[OSD([subQ0])],"isStart":true})])]});}
            var Q35;
            {var subQ0=sQuery(id+"F0.wireOp",EDGE,"E4.1.0.0");Q35=makeQuery(id+"F2.opFillet","BLEND_FACE",FACE,{"disambiguationData":[OSD([subQ0]),TDD([makeQuery(id+"F1.opExtrude","CAP_EDGE",EDGE,{"disambiguationData":[OSD([subQ0])],"isStart":true})])]});}
            var Q36;
            {var subQ0=sQuery(id+"F0.wireOp",EDGE,"E2");Q36=makeQuery(id+"F2.opFillet","BLEND_FACE",FACE,{"disambiguationData":[OSD([subQ0]),TDD([makeQuery(id+"F1.opExtrude","CAP_EDGE",EDGE,{"disambiguationData":[OSD([subQ0])],"isStart":false})])]});}
            var Q37;
            {var subQ0=sQuery(id+"F0.wireOp",EDGE,"E6.5.MirrorCS");Q37=makeQuery(id+"F2.opFillet","BLEND_FACE",FACE,{"disambiguationData":[OSD([subQ0]),TDD([makeQuery(id+"F1.opExtrude","CAP_EDGE",EDGE,{"disambiguationData":[OSD([subQ0])],"isStart":true})])]});}
            var Q38;
            {var subQ0=sQuery(id+"F0.wireOp",EDGE,"E2");Q38=makeQuery(id+"F2.opFillet","BLEND_FACE",FACE,{"disambiguationData":[OSD([subQ0]),TDD([makeQuery(id+"F1.opExtrude","CAP_EDGE",EDGE,{"disambiguationData":[OSD([subQ0])],"isStart":true})])]});}
            var Q39;
            {var subQ0=sQuery(id+"F0.wireOp",EDGE,"E1.4.0.0");Q39=makeQuery(id+"F2.opFillet","BLEND_FACE",FACE,{"disambiguationData":[OSD([subQ0]),TDD([makeQuery(id+"F1.opExtrude","CAP_EDGE",EDGE,{"disambiguationData":[OSD([subQ0])],"isStart":false})])]});}
            var Q40;
            Q40=makeQuery(id+"F1.opExtrude","CAP_FACE",FACE,{"disambiguationData":[OSD([sQuery(id+"F0.wireOp",EDGE,"E0"),sQuery(id+"F0.wireOp",EDGE,"E1.1.0.0"),sQuery(id+"F0.wireOp",EDGE,"E1.2.0.0"),sQuery(id+"F0.wireOp",EDGE,"E1.3.0.0"),sQuery(id+"F0.wireOp",EDGE,"E1.4.0.0"),sQuery(id+"F0.wireOp",EDGE,"E2"),sQuery(id+"F0.wireOp",EDGE,"E4.1.0.0"),sQuery(id+"F0.wireOp",EDGE,"E4.2.0.0"),sQuery(id+"F0.wireOp",EDGE,"E4.3.0.0"),sQuery(id+"F0.wireOp",EDGE,"E6.0.MirrorCS"),sQuery(id+"F0.wireOp",EDGE,"E6.1.MirrorCS"),sQuery(id+"F0.wireOp",EDGE,"E6.3.MirrorCS"),sQuery(id+"F0.wireOp",EDGE,"E6.4.MirrorCS"),sQuery(id+"F0.wireOp",EDGE,"E6.5.MirrorCS"),sQuery(id+"F0.wireOp",EDGE,"E6.6.MirrorCS"),sQuery(id+"F0.wireOp",EDGE,"E6.7.MirrorCS"),sQuery(id+"F0.wireOp",EDGE,"E6.8.MirrorCS"),sQuery(id+"F0.wireOp",EDGE,"E6.9.MirrorCS"),sQuery(id+"F0.wireOp",EDGE,"E7"),sQuery(id+"F0.wireOp",EDGE,"E9.0.MirrorCS")])],"isStart":false});
            var Q41;
            {var subQ0=sQuery(id+"F0.wireOp",EDGE,"E1.4.0.0");Q41=makeQuery(id+"F2.opFillet","BLEND_FACE",FACE,{"disambiguationData":[OSD([subQ0]),TDD([makeQuery(id+"F1.opExtrude","CAP_EDGE",EDGE,{"disambiguationData":[OSD([subQ0])],"isStart":true})])]});}
            var Q42;
            Q42=makeQuery(id+"F1.opExtrude","SWEPT_FACE",FACE,{"disambiguationData":[OSD([sQuery(id+"F0.wireOp",EDGE,"E6.8.MirrorCS")])]});
            var Q43;
            {var subQ0=sQuery(id+"F0.wireOp",EDGE,"E1.3.0.0");Q43=makeQuery(id+"F2.opFillet","BLEND_FACE",FACE,{"disambiguationData":[OSD([subQ0]),TDD([makeQuery(id+"F1.opExtrude","CAP_EDGE",EDGE,{"disambiguationData":[OSD([subQ0])],"isStart":true})])]});}
            var Q44;
            Q44=makeQuery(id+"F1.opExtrude","SWEPT_FACE",FACE,{"disambiguationData":[OSD([sQuery(id+"F0.wireOp",EDGE,"E6.0.MirrorCS")])]});
            var Q45;
            {var subQ0=sQuery(id+"F0.wireOp",EDGE,"E6.0.MirrorCS");Q45=makeQuery(id+"F2.opFillet","BLEND_FACE",FACE,{"disambiguationData":[OSD([subQ0]),TDD([makeQuery(id+"F1.opExtrude","CAP_EDGE",EDGE,{"disambiguationData":[OSD([subQ0])],"isStart":false})])]});}
            var Q46;
            {var subQ0=sQuery(id+"F0.wireOp",EDGE,"E4.2.0.0");Q46=makeQuery(id+"F2.opFillet","BLEND_FACE",FACE,{"disambiguationData":[OSD([subQ0]),TDD([makeQuery(id+"F1.opExtrude","CAP_EDGE",EDGE,{"disambiguationData":[OSD([subQ0])],"isStart":true})])]});}
            var Q47;
            {var subQ0=sQuery(id+"F0.wireOp",EDGE,"E0");Q47=makeQuery(id+"F2.opFillet","BLEND_FACE",FACE,{"disambiguationData":[OSD([subQ0]),TDD([makeQuery(id+"F1.opExtrude","CAP_EDGE",EDGE,{"disambiguationData":[OSD([subQ0])],"isStart":true})])]});}
            var Q48;
            {var subQ0=sQuery(id+"F0.wireOp",EDGE,"E1.1.0.0");Q48=makeQuery(id+"F2.opFillet","BLEND_FACE",FACE,{"disambiguationData":[OSD([subQ0]),TDD([makeQuery(id+"F1.opExtrude","CAP_EDGE",EDGE,{"disambiguationData":[OSD([subQ0])],"isStart":true})])]});}
            var Q49;
            {var subQ0=sQuery(id+"F0.wireOp",EDGE,"E1.1.0.0");Q49=makeQuery(id+"F2.opFillet","BLEND_FACE",FACE,{"disambiguationData":[OSD([subQ0]),TDD([makeQuery(id+"F1.opExtrude","CAP_EDGE",EDGE,{"disambiguationData":[OSD([subQ0])],"isStart":false})])]});}
            var Q50;
            {var subQ0=sQuery(id+"F0.wireOp",EDGE,"E1.2.0.0");Q50=makeQuery(id+"F2.opFillet","BLEND_FACE",FACE,{"disambiguationData":[OSD([subQ0]),TDD([makeQuery(id+"F1.opExtrude","CAP_EDGE",EDGE,{"disambiguationData":[OSD([subQ0])],"isStart":true})])]});}
            var Q51;
            Q51=makeQuery(id+"F1.opExtrude","SWEPT_FACE",FACE,{"disambiguationData":[OSD([sQuery(id+"F0.wireOp",EDGE,"E6.5.MirrorCS")])]});
            var Q52;
            {var subQ0=sQuery(id+"F0.wireOp",EDGE,"E6.3.MirrorCS");Q52=makeQuery(id+"F2.opFillet","BLEND_FACE",FACE,{"disambiguationData":[OSD([subQ0]),TDD([makeQuery(id+"F1.opExtrude","CAP_EDGE",EDGE,{"disambiguationData":[OSD([subQ0])],"isStart":false})])]});}
            var Q53;
            Q53=makeQuery(id+"F1.opExtrude","SWEPT_FACE",FACE,{"disambiguationData":[OSD([sQuery(id+"F0.wireOp",EDGE,"E6.1.MirrorCS")])]});
            var Q54;
            Q54=makeQuery(id+"F1.opExtrude","SWEPT_FACE",FACE,{"disambiguationData":[OSD([sQuery(id+"F0.wireOp",EDGE,"E9.0.MirrorCS")])]});
            var Q55;
            Q55=makeQuery(id+"F1.opExtrude","SWEPT_FACE",FACE,{"disambiguationData":[OSD([sQuery(id+"F0.wireOp",EDGE,"E1.4.0.0")])]});
            var Q56;
            {var subQ0=sQuery(id+"F0.wireOp",EDGE,"E4.3.0.0");Q56=makeQuery(id+"F2.opFillet","BLEND_FACE",FACE,{"disambiguationData":[OSD([subQ0]),TDD([makeQuery(id+"F1.opExtrude","CAP_EDGE",EDGE,{"disambiguationData":[OSD([subQ0])],"isStart":false})])]});}
            var Q57;
            {var subQ0=sQuery(id+"F0.wireOp",EDGE,"E1.3.0.0");Q57=makeQuery(id+"F2.opFillet","BLEND_FACE",FACE,{"disambiguationData":[OSD([subQ0]),TDD([makeQuery(id+"F1.opExtrude","CAP_EDGE",EDGE,{"disambiguationData":[OSD([subQ0])],"isStart":false})])]});}
            var Q58;
            {var subQ0=sQuery(id+"F0.wireOp",EDGE,"E4.2.0.0");Q58=makeQuery(id+"F2.opFillet","BLEND_FACE",FACE,{"disambiguationData":[OSD([subQ0]),TDD([makeQuery(id+"F1.opExtrude","CAP_EDGE",EDGE,{"disambiguationData":[OSD([subQ0])],"isStart":false})])]});}
            var Q59;
            {var subQ0=sQuery(id+"F0.wireOp",EDGE,"E4.1.0.0");Q59=makeQuery(id+"F2.opFillet","BLEND_FACE",FACE,{"disambiguationData":[OSD([subQ0]),TDD([makeQuery(id+"F1.opExtrude","CAP_EDGE",EDGE,{"disambiguationData":[OSD([subQ0])],"isStart":false})])]});}
            var Q60;
            {var subQ0=sQuery(id+"F0.wireOp",EDGE,"E1.2.0.0");Q60=makeQuery(id+"F2.opFillet","BLEND_FACE",FACE,{"disambiguationData":[OSD([subQ0]),TDD([makeQuery(id+"F1.opExtrude","CAP_EDGE",EDGE,{"disambiguationData":[OSD([subQ0])],"isStart":false})])]});}
            var Q61;
            {var subQ0=sQuery(id+"F0.wireOp",EDGE,"E9.0.MirrorCS");Q61=makeQuery(id+"F2.opFillet","BLEND_FACE",FACE,{"disambiguationData":[OSD([subQ0]),TDD([makeQuery(id+"F1.opExtrude","CAP_EDGE",EDGE,{"disambiguationData":[OSD([subQ0])],"isStart":false})])]});}
            var Q62;
            Q62=makeQuery(id+"F1.opExtrude","SWEPT_BODY",BODY,{"disambiguationData":[OSD([sQuery(id+"F0.wireOp",EDGE,"E0"),sQuery(id+"F0.wireOp",EDGE,"E1.1.0.0"),sQuery(id+"F0.wireOp",EDGE,"E1.2.0.0"),sQuery(id+"F0.wireOp",EDGE,"E1.3.0.0"),sQuery(id+"F0.wireOp",EDGE,"E1.4.0.0"),sQuery(id+"F0.wireOp",EDGE,"E2"),sQuery(id+"F0.wireOp",EDGE,"E4.1.0.0"),sQuery(id+"F0.wireOp",EDGE,"E4.2.0.0"),sQuery(id+"F0.wireOp",EDGE,"E4.3.0.0"),sQuery(id+"F0.wireOp",EDGE,"E6.0.MirrorCS"),sQuery(id+"F0.wireOp",EDGE,"E6.1.MirrorCS"),sQuery(id+"F0.wireOp",EDGE,"E6.3.MirrorCS"),sQuery(id+"F0.wireOp",EDGE,"E6.4.MirrorCS"),sQuery(id+"F0.wireOp",EDGE,"E6.5.MirrorCS"),sQuery(id+"F0.wireOp",EDGE,"E6.6.MirrorCS"),sQuery(id+"F0.wireOp",EDGE,"E6.7.MirrorCS"),sQuery(id+"F0.wireOp",EDGE,"E6.8.MirrorCS"),sQuery(id+"F0.wireOp",EDGE,"E6.9.MirrorCS"),sQuery(id+"F0.wireOp",EDGE,"E7"),sQuery(id+"F0.wireOp",EDGE,"E9.0.MirrorCS")])]});
            shell(context, id + "F4", {"isHollow" : true, "entities" : qUnion([Q0, Q1, Q2, Q3, Q4, Q5, Q6, Q7, Q8, Q9, Q10, Q11, Q12, Q13, Q14, Q15, Q16, Q17, Q18, Q19, Q20, Q21, Q22, Q23, Q24, Q25, Q26, Q27, Q28, Q29, Q30, Q31, Q32, Q33, Q34, Q35, Q36, Q37, Q38, Q39, Q40, Q41, Q42, Q43, Q44, Q45, Q46, Q47, Q48, Q49, Q50, Q51, Q52, Q53, Q54, Q55, Q56, Q57, Q58, Q59, Q60, Q61]), "parts" : qUnion([Q62]), "thickness" : 0.8 * mm});
        }
        {
            var Q0;
            Q0=qSketchRegion(id+"F3",true);
            extrude(context, id + "F5", {"entities" : qUnion([Q0]), "operationType" : NewBodyOperationType.REMOVE, "endBound" : BoundingType.THROUGH_ALL, "depth" : 25.4 * mm, "hasSecondDirection" : true, "secondDirectionBound" : SecondDirectionBoundingType.THROUGH_ALL, "secondDirectionOppositeDirection" : true, "secondDirectionDepth" : 25.4 * mm});
        }
        {
            var Q0;
            Q0=qCreatedBy(makeId("Top.planeOp"),FACE);
            cPlane(context, id + "F6", {"entities" : qUnion([Q0]), "cplaneType" : CPlaneType.OFFSET, "offset" : 3.3 * mm, "width" : 152.4 * mm, "height" : 152.4 * mm});
        }
        {
            var Q0;
            Q0=qCreatedBy(id+"F6.planeOp",FACE);
            var sketch = newSketch(context, id + "F7", { "sketchPlane" : qUnion([Q0])});
            skCircle(sketch, "E15", {"center": v(0, 0) * mm, "radius": 11.03 * mm});
            skLineSegment(sketch, "E16", {"start": v(0, 11.03) * mm, "end": v(59.07, 11.03) * mm, "construction": true});
            skCircle(sketch, "E17.0.1.0", {"center": v(0, 22.1) * mm, "radius": 11.03 * mm});
            skCircle(sketch, "E17.1.0.0", {"center": v(90.65, 0) * mm, "radius": 11.03 * mm});
            skCircle(sketch, "E17.1.1.0", {"center": v(90.65, 22.1) * mm, "radius": 11.03 * mm});
            skLineSegment(sketch, "E17.direction1", {"start": v(0, 0) * mm, "end": v(90.65, 0) * mm, "construction": true});
            skLineSegment(sketch, "E17.direction2", {"start": v(0, 0) * mm, "end": v(0, 22.1) * mm, "construction": true});
            skSolve(sketch);
        }
        {
            var Q0;
            Q0=qSketchRegion(id+"F7",true);
            extrude(context, id + "F8", {"entities" : qUnion([Q0]), "operationType" : NewBodyOperationType.ADD, "depth" : 37.6 * mm});
        }
    });
